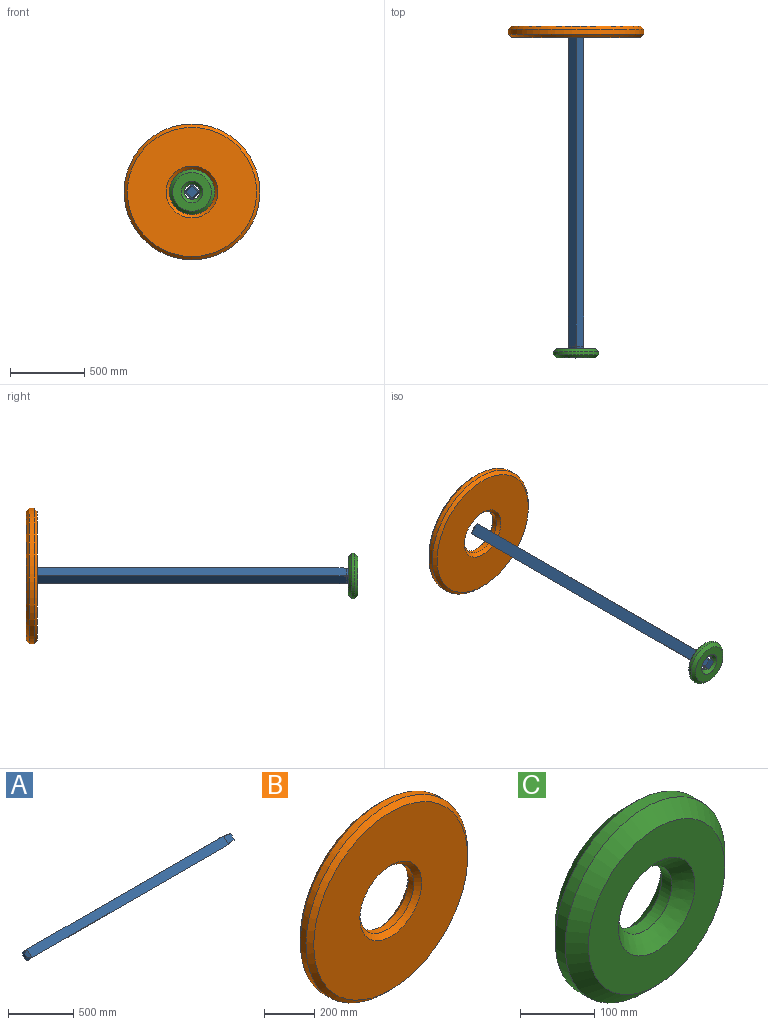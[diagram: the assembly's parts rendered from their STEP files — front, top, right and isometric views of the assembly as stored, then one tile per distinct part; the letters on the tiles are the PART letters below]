
ASSEMBLY  parts=3 mates=2
PART A: 18 faces, bbox 2235.2x107.8x107.8 mm
  f0: plane 43.11x43.11mm, normal (-1,0,0), area 929mm2, adj f14,f15,f16,f17
  f1: plane 2136.14x53.88mm, normal (0,-0.71,-0.71), area 162649.8mm2, adj f3,f4,f8,f10,f11,f15
  f2: plane 2136.14x53.88mm, normal (0,0.71,0.71), area 162649.8mm2, adj f3,f4,f6,f12,f13,f16
  f3: plane 2136.14x53.88mm, normal (0,-0.71,0.71), area 162649.8mm2, adj f1,f2,f7,f11,f12,f17
  f4: plane 2136.14x53.88mm, normal (0,0.71,-0.71), area 162649.8mm2, adj f1,f2,f5,f10,f13,f14
  f5: plane 76.2x46.66mm, normal (0.1,0.7,-0.7), area 4442.1mm2, adj f4,f9,f10,f13
  f6: plane 76.2x46.66mm, normal (0.1,0.7,0.7), area 4442.1mm2, adj f2,f9,f12,f13
  f7: plane 76.2x46.66mm, normal (0.1,-0.7,0.7), area 4442.1mm2, adj f3,f9,f11,f12
  f8: plane 76.2x46.66mm, normal (0.1,-0.7,-0.7), area 4442.1mm2, adj f1,f9,f10,f11
  f9: plane 77.89x77.89mm, normal (1,0,0), area 3569.7mm2, adj f5,f6,f7,f8,f10,f11,f12,f13
  f10: plane 100.5x14.94mm, normal (0.15,0,-0.99), area 645.2mm2, adj f1,f4,f5,f8,f9
  f11: plane 100.5x14.94mm, normal (0.15,-0.99,0), area 645.2mm2, adj f1,f3,f7,f8,f9
  f12: plane 100.5x14.94mm, normal (0.15,0,0.99), area 645.2mm2, adj f2,f3,f6,f7,f9
  f13: plane 100.5x14.94mm, normal (0.15,0.99,0), area 645.2mm2, adj f2,f4,f5,f6,f9
  f14: plane 53.88x53.88mm, normal (-0.71,0.5,-0.5), area 1724.4mm2, adj f0,f4,f15,f16
  f15: plane 53.88x53.88mm, normal (-0.71,-0.5,-0.5), area 1724.4mm2, adj f0,f1,f14,f17
  f16: plane 53.88x53.88mm, normal (-0.71,0.5,0.5), area 1724.4mm2, adj f0,f2,f14,f17
  f17: plane 53.88x53.88mm, normal (-0.71,-0.5,0.5), area 1724.4mm2, adj f0,f3,f15,f16
PART B: 8 faces, bbox 914.4x76.2x914.4 mm
  f0: cylinder r=152.4mm len=304.8mm, axis (0,1,0), area 30402.4mm2, adj f4,f6
  f1: cylinder r=457.2mm len=914.4mm, axis (0,1,0), area 91207.3mm2, adj f5,f7
  f2: plane 869.95x869.95mm, normal (0,-1,0), area 498600.2mm2, adj f6,f7
  f3: plane 869.95x869.95mm, normal (0,1,0), area 498600.2mm2, adj f4,f5
  f4: cone r=174.62mm half-angle=45deg, axis (0,1,0), area 32291.5mm2, adj f0,f3
  f5: cone r=457.2mm half-angle=45deg, axis (0,-1,0), area 88096.1mm2, adj f1,f3
  f6: cone r=152.4mm half-angle=45deg, axis (0,-1,0), area 32291.5mm2, adj f0,f2
  f7: cone r=434.98mm half-angle=45deg, axis (0,1,0), area 88096.1mm2, adj f1,f2
PART C: 8 faces, bbox 304.8x63.5x304.8 mm
  f0: cylinder r=50.8mm len=101.6mm, axis (0,1,0), area 6080.5mm2, adj f4,f6
  f1: cylinder r=152.4mm len=304.8mm, axis (0,1,0), area 18241.5mm2, adj f5,f7
  f2: plane 260.35x260.35mm, normal (0,-1,0), area 36482.9mm2, adj f4,f5
  f3: plane 260.35x260.35mm, normal (0,1,0), area 36482.9mm2, adj f6,f7
  f4: cone r=50.8mm half-angle=45deg, axis (0,-1,0), area 12226.9mm2, adj f0,f2
  f5: cone r=130.18mm half-angle=45deg, axis (0,1,0), area 27902.3mm2, adj f1,f2
  f6: cone r=73.03mm half-angle=45deg, axis (0,1,0), area 12226.9mm2, adj f0,f3
  f7: cone r=152.4mm half-angle=45deg, axis (0,-1,0), area 27902.3mm2, adj f1,f3
PLACE A rot(axis=(-0.58,0.58,-0.58),120deg) t=(-930.24,838,482.68)mm
PLACE B t=(892.48,2286.07,-305.23)mm
PLACE C t=(50.51,-12.63,-39.16)mm
MATE fastened A.f9 <-> C.f0  axis (0,-1,0) through (-213.62,-76.13,23.14)mm
MATE fastened A.f0 <-> B.f0  axis (0,1,0) through (-213.62,2159.07,23.14)mm
